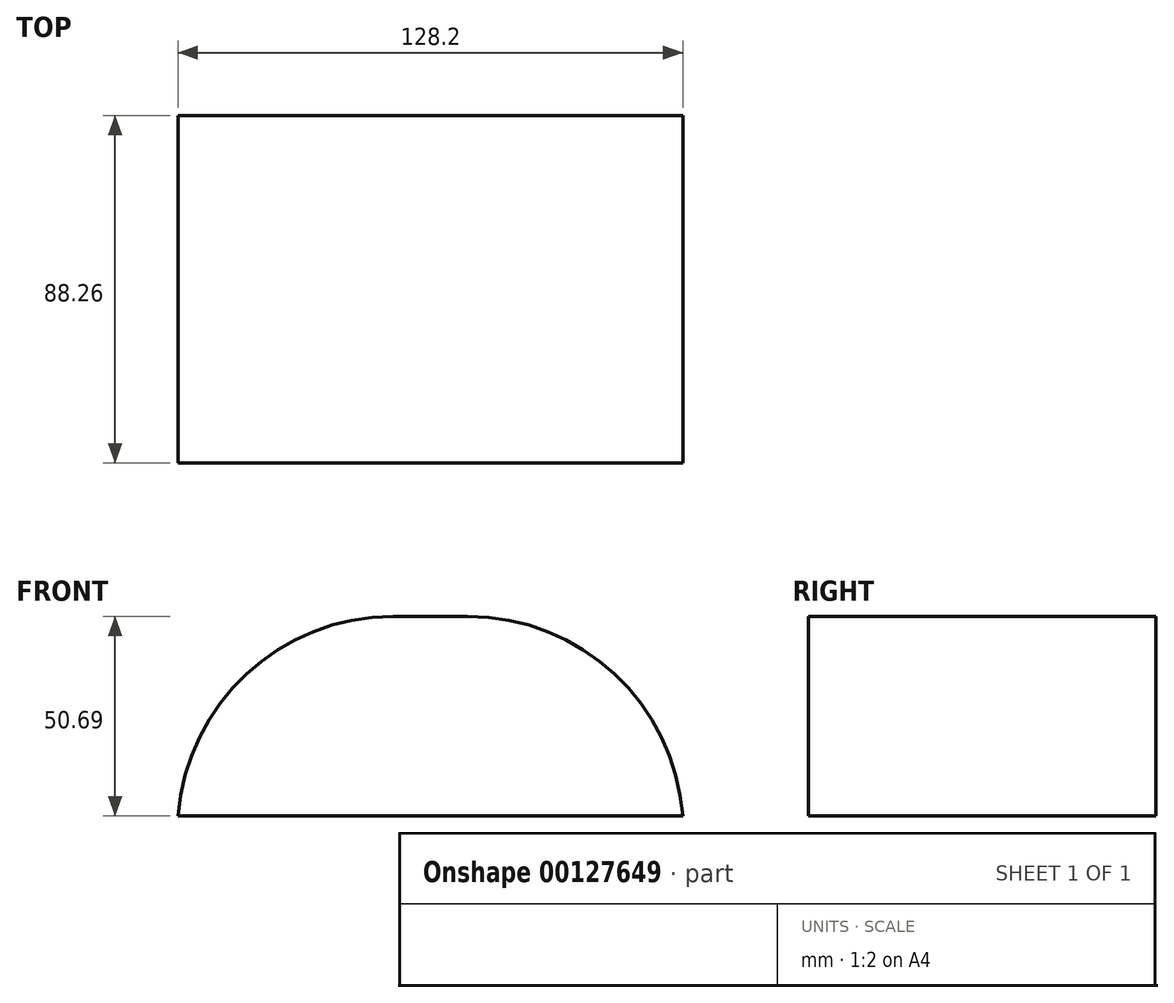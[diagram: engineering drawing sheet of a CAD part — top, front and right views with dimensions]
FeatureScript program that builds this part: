
annotation { "Feature Type Name" : "Feature", "Feature Type Description" : "" }
export const myFeature = defineFeature(function(context is Context, id is Id, definition is map)
    precondition{}
    {
        {
            var Q0;
            Q0=qCreatedBy(makeId("Top.planeOp"),FACE);
            var sketch = newSketch(context, id + "F0", { "sketchPlane" : qUnion([Q0])});
            skLineSegment(sketch, "E0.bottom", {"start": v(64.1, -44.13) * mm, "end": v(-64.1, -44.13) * mm});
            skLineSegment(sketch, "E0.top", {"start": v(64.1, 44.13) * mm, "end": v(-64.1, 44.13) * mm});
            skLineSegment(sketch, "E0.left", {"start": v(64.1, -44.13) * mm, "end": v(64.1, 44.13) * mm});
            skLineSegment(sketch, "E0.right", {"start": v(-64.1, -44.13) * mm, "end": v(-64.1, 44.13) * mm});
            skPoint(sketch, "E0.middle", {"position": v(0, 0) * mm});
            skSolve(sketch);
        }
        {
            var Q0;
            Q0 = qSketchRegion(id + "F0", true);
            extrude(context, id + "F1", {"entities" : qUnion([Q0]), "depth" : 50.69 * mm});
        }
        {
            var Q0;
            Q0=makeQuery(id+"F1.opExtrude","CAP_EDGE",EDGE,{"disambiguationData":[OSD([sQuery(id+"F0.wireOp",EDGE,"E0.right")])],"isStart":false});
            fillet(context, id + "F2", {"entities" : qUnion([Q0]), "radius" : 54.77 * mm, "tangentPropagation" : true, "allowEdgeOverflow" : false});
        }
        {
            var Q0;
            Q0=makeQuery(id+"F1.opExtrude","CAP_EDGE",EDGE,{"disambiguationData":[OSD([sQuery(id+"F0.wireOp",EDGE,"E0.left")])],"isStart":false});
            fillet(context, id + "F3", {"entities" : qUnion([Q0]), "radius" : 54.77 * mm, "tangentPropagation" : true, "allowEdgeOverflow" : false});
        }
    });
